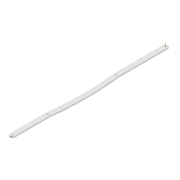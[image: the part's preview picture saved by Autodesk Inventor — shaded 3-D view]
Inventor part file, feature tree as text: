
AUTODESK INVENTOR PART (.ipt)
format: ipt  version: 2022 (Build 260153000, 153)  size: 102,912 bytes
history: native  units: mm
features: extrude x1, other x1, sketch x1
ambient origin geometry x8: Origin, YZ Plane, XZ Plane, XY Plane, X Axis, Y Axis, Z Axis, Center Point
bodies: Solid1 (feature_tree)
feature tree (3):
  extrude  "Extrusion1"  Depth=600.0mm
  other  "Work Axis3"
  sketch  "Sketch1"  dims[d0=3.3mm d1=3.3mm d2=10.0mm d3=322.934mm d4=3.3mm d5=74.182mm d6=3.0mm d7=0.0mm d8=3.3mm d9=218.733mm d12=600.0mm d13=600.0mm]
